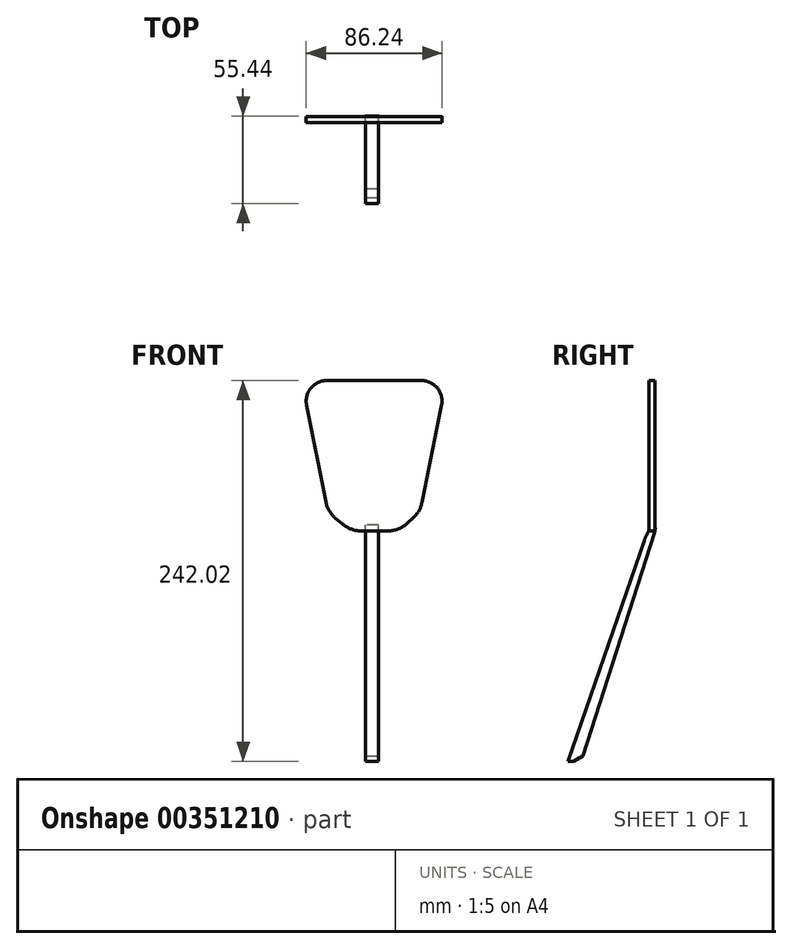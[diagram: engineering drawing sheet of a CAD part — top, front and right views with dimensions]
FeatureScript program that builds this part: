
annotation { "Feature Type Name" : "Feature", "Feature Type Description" : "" }
export const myFeature = defineFeature(function(context is Context, id is Id, definition is map)
    precondition{}
    {
        {
            var Q0;
            Q0=qCreatedBy(makeId("Front.planeOp"),FACE);
            var sketch = newSketch(context, id + "F0", { "sketchPlane" : qUnion([Q0])});
            skLineSegment(sketch, "E0", {"start": v(-32.32, -28.34) * mm, "end": v(26.32, -28.34) * mm});
            skLineSegment(sketch, "E1", {"start": v(26.32, -28.34) * mm, "end": v(41.4, 46.35) * mm});
            skLineSegment(sketch, "E2", {"start": v(-47.17, 46.4) * mm, "end": v(-32.32, -28.34) * mm});
            skLineSegment(sketch, "E3", {"start": v(-47.17, 46.4) * mm, "end": v(-37.74, 54.9) * mm});
            skLineSegment(sketch, "E4", {"start": v(-37.74, 54.9) * mm, "end": v(32.02, 54.9) * mm});
            skLineSegment(sketch, "E5", {"start": v(32.02, 54.9) * mm, "end": v(41.4, 46.35) * mm});
            skLineSegment(sketch, "E6", {"start": v(-32.32, -28.34) * mm, "end": v(-17.78, -40.67) * mm});
            skLineSegment(sketch, "E7", {"start": v(-17.78, -40.67) * mm, "end": v(12.9, -40.67) * mm});
            skLineSegment(sketch, "E8", {"start": v(12.9, -40.67) * mm, "end": v(26.32, -28.34) * mm});
            skSolve(sketch);
        }
        {
            var Q0;
            Q0=makeQuery(id+"F0.imprint","IMPRINT",FACE,{"disambiguationData":[TD([[makeQuery(id+"F0.imprint","IMPRINT",EDGE,{"derivedFrom":sQuery(id+"F0.wireOp",EDGE,"E0")}),1.0]])]});
            extrude(context, id + "F1", {"entities" : qUnion([Q0]), "depth" : 3.56 * mm});
        }
        {
            var Q0;
            Q0=makeQuery(id+"F1.opExtrude","SWEPT_EDGE",EDGE,{"disambiguationData":[OSD([sQuery(id+"F0.wireOp",EDGE,"Fk8r7551-bc7v-8mNO-zMRn-gDDcsifaMFvY"),sQuery(id+"F0.wireOp",EDGE,"E2")])]});
            fillet(context, id + "F2", {"entities" : qUnion([Q0]), "radius" : 12.7 * mm, "tangentPropagation" : true, "allowEdgeOverflow" : false});
        }
        {
            var Q0;
            Q0=makeQuery(id+"F1.opExtrude","SWEPT_EDGE",EDGE,{"disambiguationData":[OSD([sQuery(id+"F0.wireOp",EDGE,"E1"),sQuery(id+"F0.wireOp",EDGE,"E5")])]});
            fillet(context, id + "F3", {"entities" : qUnion([Q0]), "radius" : 12.7 * mm, "tangentPropagation" : true, "allowEdgeOverflow" : false});
        }
        {
            var Q0;
            Q0=makeQuery(id+"F1.opExtrude","SWEPT_EDGE",EDGE,{"disambiguationData":[OSD([sQuery(id+"F0.wireOp",EDGE,"E4"),sQuery(id+"F0.wireOp",EDGE,"E5")])]});
            var Q1;
            Q1=makeQuery(id+"F1.opExtrude","SWEPT_EDGE",EDGE,{"disambiguationData":[OSD([sQuery(id+"F0.wireOp",EDGE,"E3"),sQuery(id+"F0.wireOp",EDGE,"E4")])]});
            fillet(context, id + "F4", {"entities" : qUnion([Q0, Q1]), "radius" : 14.22 * mm, "tangentPropagation" : true, "allowEdgeOverflow" : false});
        }
        {
            var Q0;
            Q0=makeQuery(id+"F1.opExtrude","SWEPT_EDGE",EDGE,{"disambiguationData":[OSD([sQuery(id+"F0.wireOp",EDGE,"E0"),sQuery(id+"F0.wireOp",EDGE,"E1")])]});
            fillet(context, id + "F5", {"entities" : qUnion([Q0]), "radius" : 13.04 * mm, "tangentPropagation" : true, "allowEdgeOverflow" : false});
        }
        {
            var Q0;
            Q0=makeQuery(id+"F0.imprint","IMPRINT",FACE,{"disambiguationData":[TD([[makeQuery(id+"F0.imprint","IMPRINT",EDGE,{"derivedFrom":sQuery(id+"F0.wireOp",EDGE,"E0")}),-1.0]])]});
            var Q1;
            Q1=makeQuery(id+"F0.imprint","IMPRINT",FACE,{"disambiguationData":[TD([[makeQuery(id+"F0.imprint","IMPRINT",EDGE,{"derivedFrom":sQuery(id+"F0.wireOp",EDGE,"E0")}),1.0]])]});
            extrude(context, id + "F6", {"entities" : qUnion([Q0, Q1]), "operationType" : NewBodyOperationType.ADD, "depth" : 3.8 * mm});
        }
        {
            var Q0;
            Q0=makeQuery(id+"F6.opExtrude","SWEPT_EDGE",EDGE,{"disambiguationData":[OSD([sQuery(id+"F0.wireOp",EDGE,"E4"),sQuery(id+"F0.wireOp",EDGE,"E5")])]});
            var Q1;
            Q1=makeQuery(id+"F6.opExtrude","SWEPT_EDGE",EDGE,{"disambiguationData":[OSD([sQuery(id+"F0.wireOp",EDGE,"E1"),sQuery(id+"F0.wireOp",EDGE,"E5")])]});
            var Q2;
            Q2=makeQuery(id+"F6.opExtrude","SWEPT_EDGE",EDGE,{"disambiguationData":[OSD([sQuery(id+"F0.wireOp",EDGE,"E3"),sQuery(id+"F0.wireOp",EDGE,"E4")])]});
            var Q3;
            Q3=makeQuery(id+"F6.opExtrude","SWEPT_EDGE",EDGE,{"disambiguationData":[OSD([sQuery(id+"F0.wireOp",EDGE,"E2"),sQuery(id+"F0.wireOp",EDGE,"E3")])]});
            fillet(context, id + "F7", {"entities" : qUnion([Q0, Q1, Q2, Q3]), "radius" : 12.7 * mm, "tangentPropagation" : true, "allowEdgeOverflow" : false});
        }
        {
            var Q0;
            Q0=makeQuery(id+"F6.opExtrude","SWEPT_EDGE",EDGE,{"disambiguationData":[OSD([sQuery(id+"F0.wireOp",EDGE,"E6"),sQuery(id+"F0.wireOp",EDGE,"E7")])]});
            var Q1;
            Q1=makeQuery(id+"F6.opExtrude","SWEPT_EDGE",EDGE,{"disambiguationData":[OSD([sQuery(id+"F0.wireOp",EDGE,"E7"),sQuery(id+"F0.wireOp",EDGE,"E8")])]});
            var Q2;
            Q2=makeQuery(id+"F6.opExtrude","SWEPT_EDGE",EDGE,{"disambiguationData":[OSD([sQuery(id+"F0.wireOp",EDGE,"E0"),sQuery(id+"F0.wireOp",EDGE,"E1"),sQuery(id+"F0.wireOp",EDGE,"E8")])]});
            var Q3;
            {var subQ0=sQuery(id+"F0.wireOp",EDGE,"E6");var subQ1=sQuery(id+"F0.wireOp",EDGE,"E2");var subQ2=sQuery(id+"F0.wireOp",EDGE,"E0");Q3=makeQuery(id+"F6.boolean.opBoolean","MERGE",EDGE,{"derivedFrom":[makeQuery(id+"F1.opExtrude","SWEPT_EDGE",EDGE,{"disambiguationData":[OSD([subQ2,subQ1,subQ0])]}),makeQuery(id+"F6.opExtrude","SWEPT_EDGE",EDGE,{"disambiguationData":[OSD([subQ2,subQ1,subQ0])]})]});}
            fillet(context, id + "F8", {"entities" : qUnion([Q0, Q1, Q2, Q3]), "radius" : 17.78 * mm, "tangentPropagation" : true, "allowEdgeOverflow" : false});
        }
        {
            var Q0;
            Q0=qCreatedBy(makeId("Right.planeOp"),FACE);
            var sketch = newSketch(context, id + "F9", { "sketchPlane" : qUnion([Q0])});
            skPoint(sketch, "E9.start.orphan", {"position": v(0, -37.73) * mm});
            skLineSegment(sketch, "E10", {"start": v(0, -37.73) * mm, "end": v(-51.62, -187.1) * mm});
            skLineSegment(sketch, "E11", {"start": v(-51.62, -187.1) * mm, "end": v(-45.78, -183.6) * mm});
            skLineSegment(sketch, "E12", {"start": v(-45.78, -183.6) * mm, "end": v(2.15, -34.65) * mm});
            skLineSegment(sketch, "E13", {"start": v(2.15, -34.65) * mm, "end": v(-4.98, -41.84) * mm});
            skLineSegment(sketch, "E14", {"start": v(-4.98, -41.84) * mm, "end": v(-55.18, -187.1) * mm});
            skLineSegment(sketch, "E15", {"start": v(-55.18, -187.1) * mm, "end": v(-51.62, -187.1) * mm});
            skSolve(sketch);
        }
        {
            var Q0;
            Q0=makeQuery(id+"F9.imprint","IMPRINT",FACE,{"disambiguationData":[TD([[makeQuery(id+"F9.imprint","IMPRINT",EDGE,{"derivedFrom":sQuery(id+"F9.wireOp",EDGE,"E11")}),1.0]])]});
            extrude(context, id + "F10", {"entities" : qUnion([Q0]), "operationType" : NewBodyOperationType.ADD, "oppositeDirection" : true, "depth" : 8.38 * mm});
        }
        {
            var Q0;
            Q0=makeQuery(id+"F10.opExtrude","SWEPT_EDGE",EDGE,{"disambiguationData":[OSD([sQuery(id+"F9.wireOp",EDGE,"E12"),sQuery(id+"F9.wireOp",EDGE,"E13")])]});
            fillet(context, id + "F11", {"entities" : qUnion([Q0]), "radius" : 9.63 * mm, "tangentPropagation" : true, "allowEdgeOverflow" : false});
        }
        {
            var Q0;
            Q0=makeQuery(id+"F10.opExtrude","SWEPT_EDGE",EDGE,{"disambiguationData":[OSD([sQuery(id+"F9.wireOp",EDGE,"E13"),sQuery(id+"F9.wireOp",EDGE,"E14")])]});
            fillet(context, id + "F12", {"entities" : qUnion([Q0]), "radius" : 29.68 * mm, "tangentPropagation" : true, "allowEdgeOverflow" : false});
        }
    });
